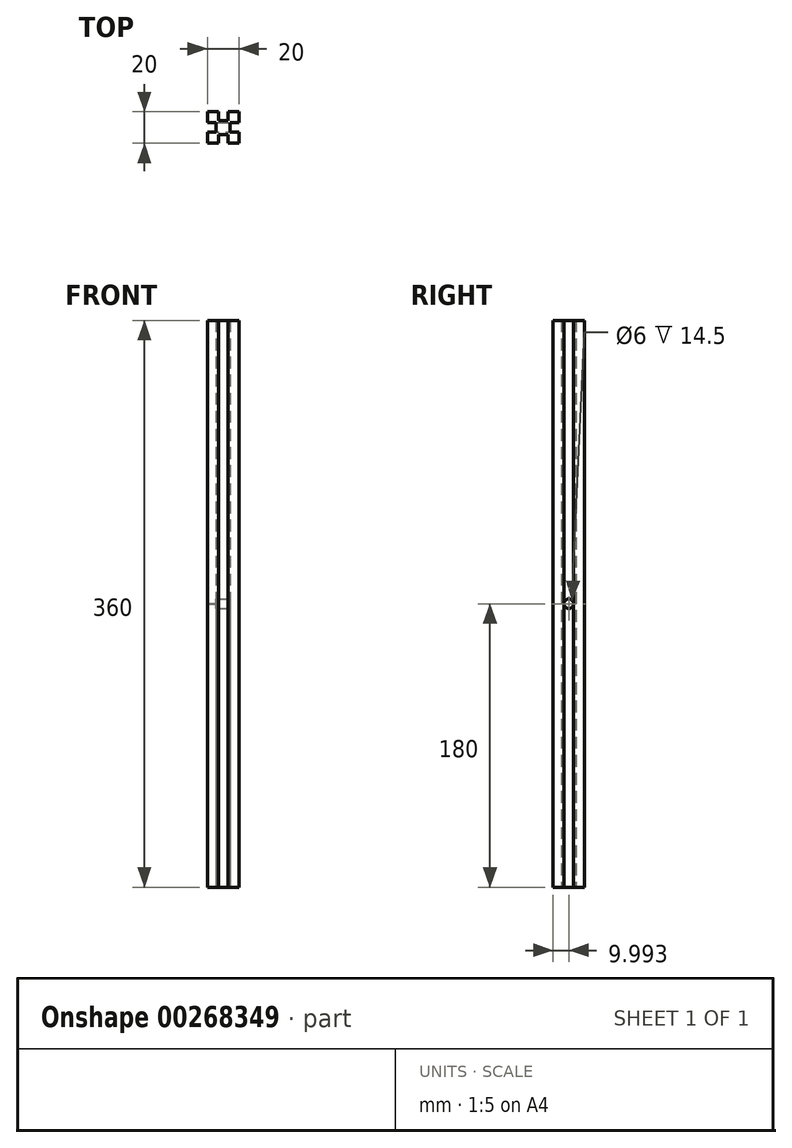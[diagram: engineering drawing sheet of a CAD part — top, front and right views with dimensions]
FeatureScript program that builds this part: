
annotation { "Feature Type Name" : "Feature", "Feature Type Description" : "" }
export const myFeature = defineFeature(function(context is Context, id is Id, definition is map)
    precondition{}
    {
        {
            var Q0;
            Q0=qCreatedBy(makeId("Top.planeOp"),FACE);
            var sketch = newSketch(context, id + "F0", { "sketchPlane" : qUnion([Q0])});
            skLineSegment(sketch, "E0.bottom", {"start": v(0, 0) * mm, "end": v(20, 0) * mm});
            skLineSegment(sketch, "E0.top", {"start": v(0, 20) * mm, "end": v(20, 20) * mm});
            skLineSegment(sketch, "E0.left", {"start": v(0, 0) * mm, "end": v(0, 20) * mm});
            skLineSegment(sketch, "E0.right", {"start": v(20, 0) * mm, "end": v(20, 20) * mm});
            skLineSegment(sketch, "E1.bottom", {"start": v(7, 20) * mm, "end": v(13, 20) * mm});
            skLineSegment(sketch, "E1.top", {"start": v(7, 14.5) * mm, "end": v(13, 14.5) * mm});
            skLineSegment(sketch, "E1.left", {"start": v(7, 20) * mm, "end": v(7, 14.5) * mm});
            skLineSegment(sketch, "E1.right", {"start": v(13, 20) * mm, "end": v(13, 14.5) * mm});
            skLineSegment(sketch, "E2.bottom", {"start": v(20, 13) * mm, "end": v(14.5, 13) * mm});
            skLineSegment(sketch, "E2.top", {"start": v(20, 7) * mm, "end": v(14.5, 7) * mm});
            skLineSegment(sketch, "E2.left", {"start": v(20, 13) * mm, "end": v(20, 7) * mm});
            skLineSegment(sketch, "E2.right", {"start": v(14.5, 13) * mm, "end": v(14.5, 7) * mm});
            skLineSegment(sketch, "E3.bottom", {"start": v(13, 0) * mm, "end": v(7, 0) * mm});
            skLineSegment(sketch, "E3.top", {"start": v(13, 5.5) * mm, "end": v(7, 5.5) * mm});
            skLineSegment(sketch, "E3.left", {"start": v(13, 0) * mm, "end": v(13, 5.5) * mm});
            skLineSegment(sketch, "E3.right", {"start": v(7, 0) * mm, "end": v(7, 5.5) * mm});
            skLineSegment(sketch, "E4.bottom", {"start": v(0, 7) * mm, "end": v(5.5, 7) * mm});
            skLineSegment(sketch, "E4.top", {"start": v(0, 13) * mm, "end": v(5.5, 13) * mm});
            skLineSegment(sketch, "E4.left", {"start": v(0, 7) * mm, "end": v(0, 13) * mm});
            skLineSegment(sketch, "E4.right", {"start": v(5.5, 7) * mm, "end": v(5.5, 13) * mm});
            skSolve(sketch);
        }
        {
            var Q0;
            Q0=makeQuery(id+"F0.imprint","IMPRINT",FACE,{"disambiguationData":[TD([[makeQuery(id+"F0.imprint","IMPRINT",EDGE,{"derivedFrom":sQuery(id+"F0.wireOp",EDGE,"E1.top")}),-1.0]])]});
            extrude(context, id + "F1", {"entities" : qUnion([Q0]), "depth" : 360 * mm});
        }
        {
            var Q0;
            Q0=makeQuery(id+"F1.opExtrude","SWEPT_FACE",FACE,{"disambiguationData":[OSD([sQuery(id+"F0.wireOp",EDGE,"E2.right")])]});
            var sketch = newSketch(context, id + "F2", { "sketchPlane" : qUnion([Q0])});
            skCircle(sketch, "E5", {"center": v(10, 180) * mm, "radius": 3 * mm});
            skPoint(sketch, "E5.centerSnap0", {"position": v(13, 180) * mm});
            skSolve(sketch);
        }
        {
            var Q0;
            Q0=qSketchRegion(id+"F2",true);
            extrude(context, id + "F3", {"entities" : qUnion([Q0]), "operationType" : NewBodyOperationType.REMOVE, "oppositeDirection" : true, "depth" : 25 * mm});
        }
    });
